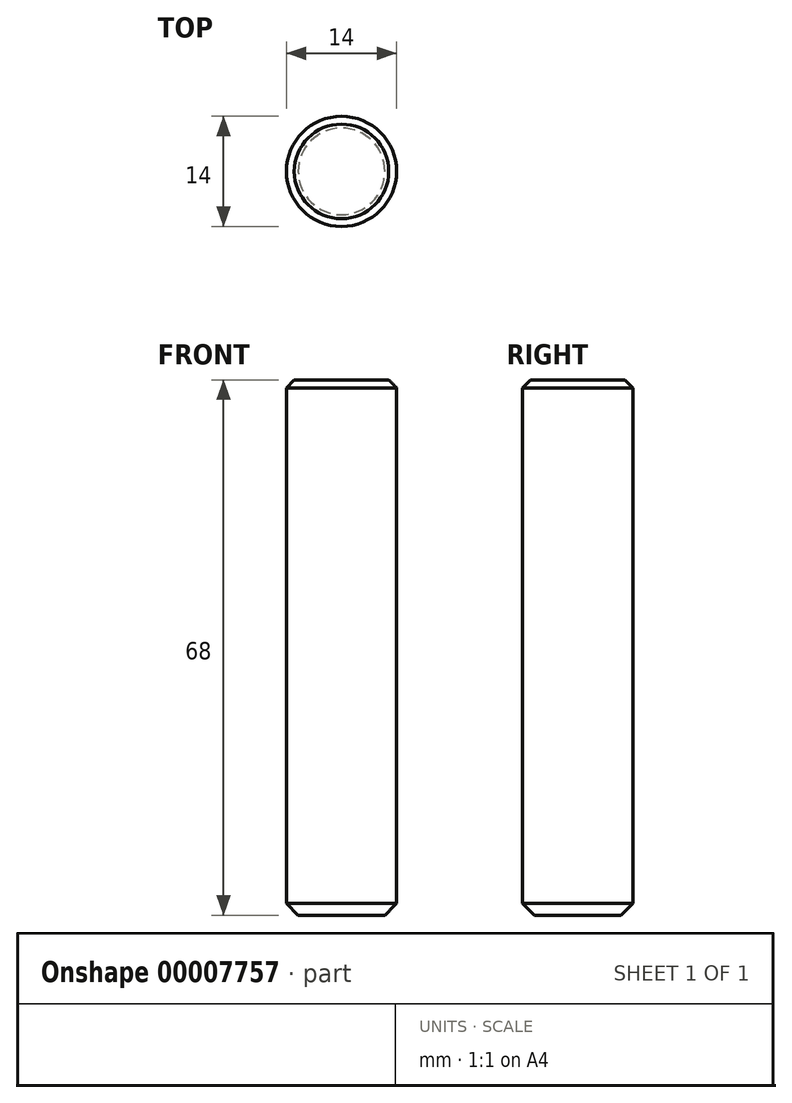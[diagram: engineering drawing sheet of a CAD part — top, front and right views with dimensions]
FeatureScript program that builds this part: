
annotation { "Feature Type Name" : "Feature", "Feature Type Description" : "" }
export const myFeature = defineFeature(function(context is Context, id is Id, definition is map)
    precondition{}
    {
        {
            var Q0;
            Q0=qCreatedBy(makeId("Top.planeOp"),FACE);
            var sketch = newSketch(context, id + "F0", { "sketchPlane" : qUnion([Q0])});
            skCircle(sketch, "E0", {"center": v(0, 0) * mm, "radius": 7 * mm});
            skSolve(sketch);
        }
        {
            var Q0;
            Q0 = qSketchRegion(id + "F0", true);
            extrude(context, id + "F1", {"entities" : qUnion([Q0]), "endBound" : BoundingType.SYMMETRIC, "depth" : 68 * mm});
        }
        {
            var Q0;
            Q0=makeQuery(id+"F1.opExtrude","CAP_EDGE",EDGE,{"disambiguationData":[OSD([sQuery(id+"F0.wireOp",EDGE,"E0")])],"isStart":false});
            chamfer(context, id + "F2", {"entities" : qUnion([Q0]), "width" : 1 * mm, "tangentPropagation" : true});
        }
        {
            var Q0;
            Q0=makeQuery(id+"F1.opExtrude","CAP_EDGE",EDGE,{"disambiguationData":[OSD([sQuery(id+"F0.wireOp",EDGE,"E0")])],"isStart":true});
            chamfer(context, id + "F3", {"entities" : qUnion([Q0]), "width" : 1.5 * mm, "tangentPropagation" : true});
        }
    });
